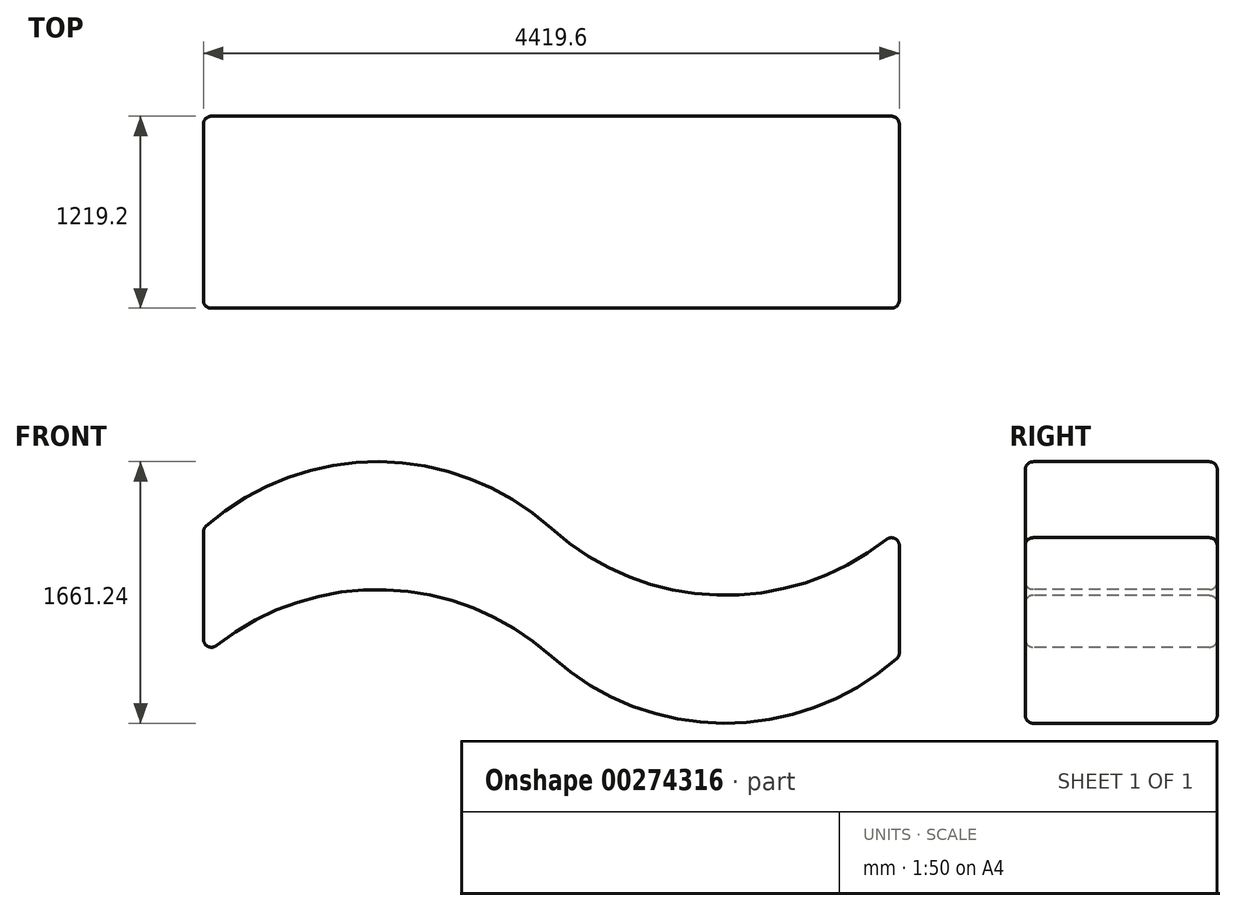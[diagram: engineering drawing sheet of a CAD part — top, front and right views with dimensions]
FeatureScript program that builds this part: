
annotation { "Feature Type Name" : "Feature", "Feature Type Description" : "" }
export const myFeature = defineFeature(function(context is Context, id is Id, definition is map)
    precondition{}
    {
        {
            var Q0;
            Q0=qCreatedBy(makeId("Front.planeOp"),FACE);
            var sketch = newSketch(context, id + "F0", { "sketchPlane" : qUnion([Q0])});
            skLineSegment(sketch, "E0", {"start": v(2209.8, 0) * mm, "end": v(2209.8, 812.8) * mm});
            skPoint(sketch, "E1", {"position": v(1104.9, 1226.78) * mm});
            skArc(sketch, "E2", {"start": v(2209.8, 0) * mm, "mid": v(1104.9, -424.22) * mm, "end": v(0, 0) * mm});
            skLineSegment(sketch, "E3", {"start": v(-2209.8, 812.8) * mm, "end": v(-2209.8, 0) * mm});
            skArc(sketch, "E4", {"start": v(0, 812.8) * mm, "mid": v(-1104.9, 1237.02) * mm, "end": v(-2209.8, 812.8) * mm});
            skArc(sketch, "E5", {"start": v(0, 0) * mm, "mid": v(-1104.9, 424.22) * mm, "end": v(-2209.8, 0) * mm});
            skArc(sketch, "E6", {"start": v(0, 812.8) * mm, "mid": v(1104.9, 388.58) * mm, "end": v(2209.8, 812.8) * mm});
            skSolve(sketch);
        }
        {
            var Q0;
            Q0 = qSketchRegion(id + "F0", true);
            extrude(context, id + "F1", {"entities" : qUnion([Q0]), "oppositeDirection" : true, "depth" : 1219.2 * mm});
        }
        {
            var Q0;
            Q0=makeQuery(id+"F1.opExtrude","CAP_FACE",FACE,{"disambiguationData":[OSD([sQuery(id+"F0.wireOp",EDGE,"E0"),sQuery(id+"F0.wireOp",EDGE,"E2"),sQuery(id+"F0.wireOp",EDGE,"E3"),sQuery(id+"F0.wireOp",EDGE,"E4"),sQuery(id+"F0.wireOp",EDGE,"E5"),sQuery(id+"F0.wireOp",EDGE,"E6")])],"isStart":false});
            var Q1;
            Q1=makeQuery(id+"F1.opExtrude","SWEPT_FACE",FACE,{"disambiguationData":[OSD([sQuery(id+"F0.wireOp",EDGE,"E3")])]});
            var Q2;
            Q2=makeQuery(id+"F1.opExtrude","CAP_FACE",FACE,{"disambiguationData":[OSD([sQuery(id+"F0.wireOp",EDGE,"E0"),sQuery(id+"F0.wireOp",EDGE,"E2"),sQuery(id+"F0.wireOp",EDGE,"E3"),sQuery(id+"F0.wireOp",EDGE,"E4"),sQuery(id+"F0.wireOp",EDGE,"E5"),sQuery(id+"F0.wireOp",EDGE,"E6")])],"isStart":true});
            var Q3;
            Q3=makeQuery(id+"F1.opExtrude","SWEPT_FACE",FACE,{"disambiguationData":[OSD([sQuery(id+"F0.wireOp",EDGE,"E0")])]});
            fillet(context, id + "F2", {"entities" : qUnion([Q0, Q1, Q2, Q3]), "radius" : 50.8 * mm, "tangentPropagation" : true, "allowEdgeOverflow" : false});
        }
    });
